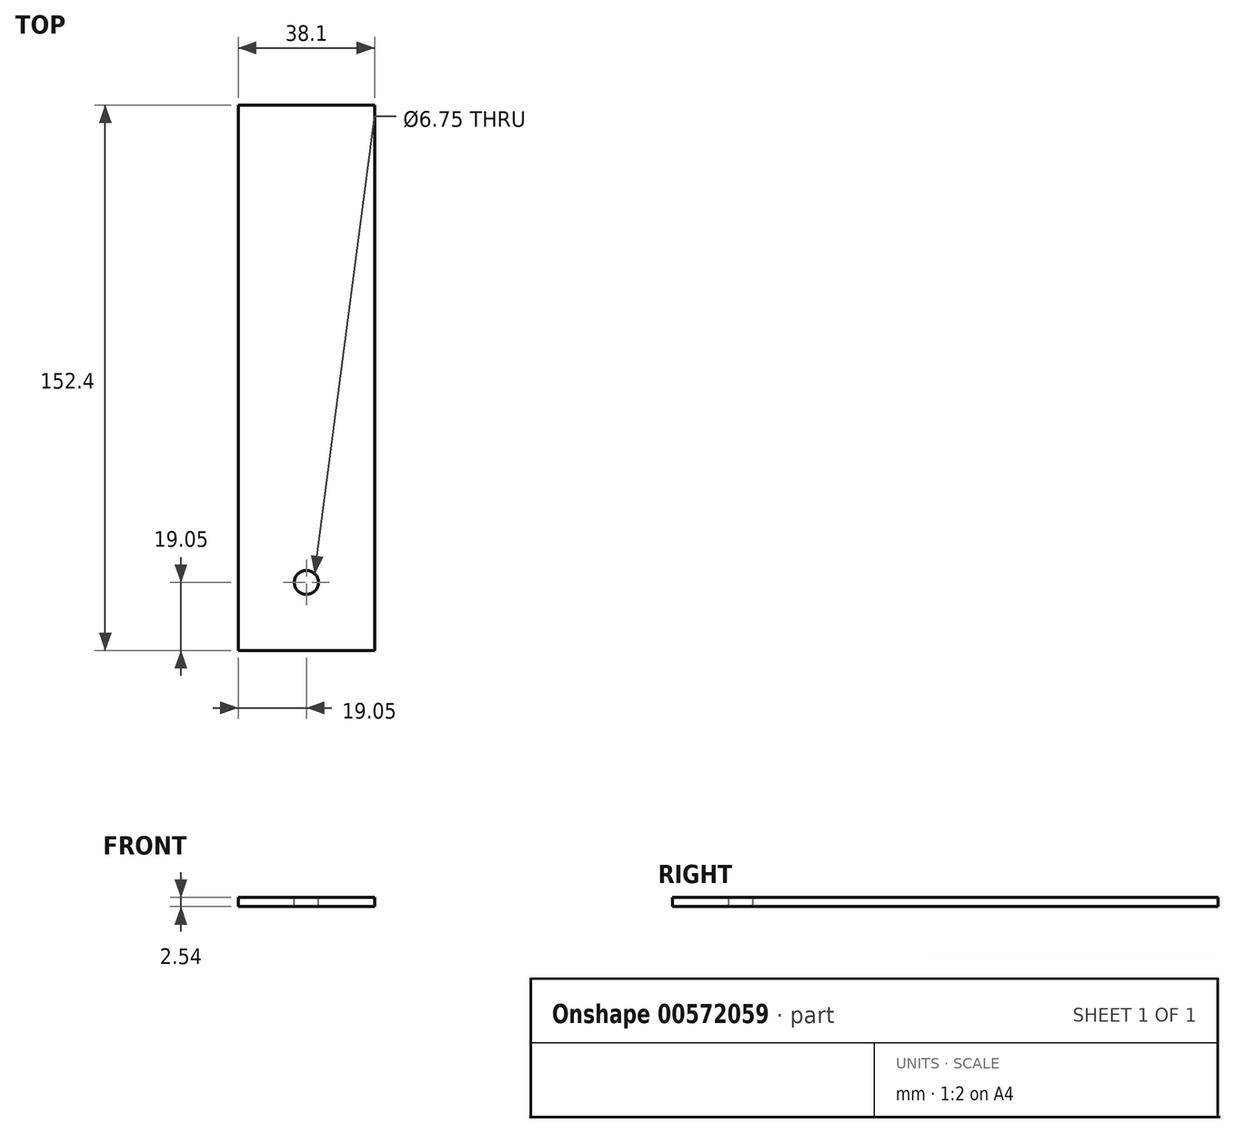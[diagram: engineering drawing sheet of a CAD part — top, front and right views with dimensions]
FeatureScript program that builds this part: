
annotation { "Feature Type Name" : "Feature", "Feature Type Description" : "" }
export const myFeature = defineFeature(function(context is Context, id is Id, definition is map)
    precondition{}
    {
        {
            var Q0;
            Q0=qCreatedBy(makeId("Top.planeOp"),FACE);
            var sketch = newSketch(context, id + "F0", { "sketchPlane" : qUnion([Q0])});
            skLineSegment(sketch, "E0.bottom", {"start": v(19.05, 76.2) * mm, "end": v(-19.05, 76.2) * mm});
            skLineSegment(sketch, "E0.top", {"start": v(19.05, -76.2) * mm, "end": v(-19.05, -76.2) * mm});
            skLineSegment(sketch, "E0.left", {"start": v(19.05, 76.2) * mm, "end": v(19.05, -76.2) * mm});
            skLineSegment(sketch, "E0.right", {"start": v(-19.05, 76.2) * mm, "end": v(-19.05, -76.2) * mm});
            skPoint(sketch, "E0.middle", {"position": v(0, 0) * mm});
            skSolve(sketch);
        }
        {
            var Q0;
            Q0=makeQuery(id+"F0.imprint","IMPRINT",FACE,{"disambiguationData":[TD([[makeQuery(id+"F0.imprint","IMPRINT",EDGE,{"derivedFrom":sQuery(id+"F0.wireOp",EDGE,"E0.bottom")}),1.0]])]});
            extrude(context, id + "F1", {"entities" : qUnion([Q0]), "depth" : 2.54 * mm, "offsetDistance" : 25.4 * mm});
        }
        {
            var Q0;
            Q0=makeQuery(id+"F1.opExtrude","CAP_FACE",FACE,{"disambiguationData":[OSD([sQuery(id+"F0.wireOp",EDGE,"E0.bottom"),sQuery(id+"F0.wireOp",EDGE,"E0.top"),sQuery(id+"F0.wireOp",EDGE,"E0.left"),sQuery(id+"F0.wireOp",EDGE,"E0.right")])],"isStart":false});
            var sketch = newSketch(context, id + "F2", { "sketchPlane" : qUnion([Q0])});
            skPoint(sketch, "E1", {"position": v(0, -57.15) * mm});
            skPoint(sketch, "E1.positionSnap0", {"position": v(0, -76.2) * mm});
            skSolve(sketch);
        }
        {
            var Q0;
            Q0=sQuery(id+"F2.wireOp",VERTEX,"E1");
            var Q1;
            Q1=makeQuery(id+"F1.opExtrude","SWEPT_BODY",BODY,{"disambiguationData":[OSD([sQuery(id+"F0.wireOp",EDGE,"E0.bottom"),sQuery(id+"F0.wireOp",EDGE,"E0.top"),sQuery(id+"F0.wireOp",EDGE,"E0.left"),sQuery(id+"F0.wireOp",EDGE,"E0.right")])]});
            hole(context, id + "F3", {"style" : HoleStyle.SIMPLE, "endStyle" : HoleEndStyle.THROUGH, "holeDiameter" : 6.75 * mm, "majorDiameter" : 6.35 * mm, "isTappedThrough" : true, "tappedDepth" : 12.7 * mm, "tapClearance" : 3, "locations" : qUnion([Q0]), "scope" : qUnion([Q1])});
        }
    });
